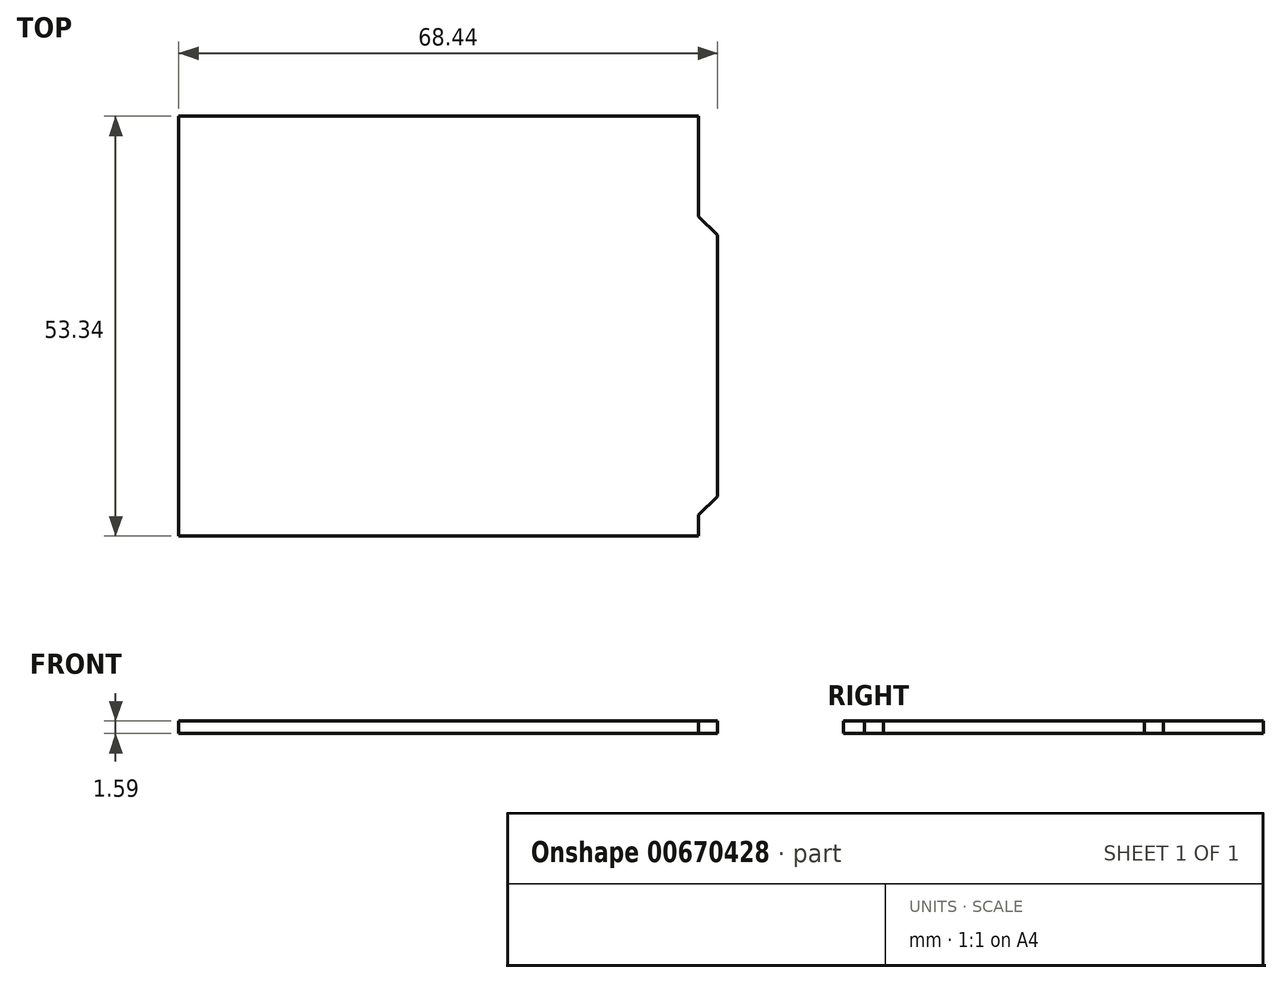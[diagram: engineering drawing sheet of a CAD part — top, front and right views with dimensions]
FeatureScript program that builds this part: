
annotation { "Feature Type Name" : "Feature", "Feature Type Description" : "" }
export const myFeature = defineFeature(function(context is Context, id is Id, definition is map)
    precondition{}
    {
        {
            var Q0;
            Q0=qCreatedBy(makeId("Top.planeOp"),FACE);
            var sketch = newSketch(context, id + "F0", { "sketchPlane" : qUnion([Q0])});
            skLineSegment(sketch, "E0", {"start": v(0, 53.34) * mm, "end": v(66.04, 53.34) * mm});
            skLineSegment(sketch, "E1", {"start": v(66.04, 53.34) * mm, "end": v(66.04, 40.63) * mm});
            skLineSegment(sketch, "E2", {"start": v(0, 53.34) * mm, "end": v(0, 0) * mm});
            skLineSegment(sketch, "E3", {"start": v(0, 0) * mm, "end": v(66.04, 0) * mm});
            skLineSegment(sketch, "E4", {"start": v(66.04, 40.63) * mm, "end": v(68.44, 38.23) * mm});
            skLineSegment(sketch, "E5", {"start": v(68.44, 38.23) * mm, "end": v(68.44, 5.07) * mm});
            skLineSegment(sketch, "E6", {"start": v(68.44, 5.07) * mm, "end": v(66.04, 2.67) * mm});
            skLineSegment(sketch, "E7.trimOffspring", {"start": v(66.04, 2.67) * mm, "end": v(66.04, 0) * mm});
            skSolve(sketch);
        }
        {
            var Q0;
            Q0=makeQuery(id+"F0.imprint","IMPRINT",FACE,{"disambiguationData":[TD([[makeQuery(id+"F0.imprint","IMPRINT",EDGE,{"derivedFrom":sQuery(id+"F0.wireOp",EDGE,"E0")}),-1.0]])]});
            extrude(context, id + "F1", {"entities" : qUnion([Q0]), "depth" : 1.59 * mm, "offsetDistance" : 25 * mm});
        }
    });
